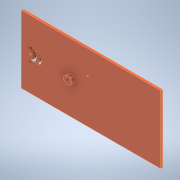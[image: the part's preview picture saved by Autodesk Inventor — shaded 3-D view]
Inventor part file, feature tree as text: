
AUTODESK INVENTOR PART (.ipt)
format: ipt  version: 2022.2 (Build 262287010, 287A)  size: 254,976 bytes
history: native  units: mm
features: extrude x15, sketch x9, other x1, plane x1
ambient origin geometry x8: Origin, YZ Plane, XZ Plane, XY Plane, X Axis, Y Axis, Z Axis, Center Point
bodies: Body1 (feature_tree)
feature tree (26):
  other  "Sólido1"
  extrude  "Extrusión1"  Depth=170.0mm
  extrude  "Extrusión4"  Depth=5.0mm
  extrude  "Extrusión5"  Depth=85.0mm
  extrude  "Extrusión6"  Depth=5.25mm
  sketch  "Boceto10"  dims[d26=4.0mm d27=0.0mm d29=50.0mm]
  plane  "Plano de trabajo1"
  extrude  "Extrusión10"  Depth=4.0mm
  extrude  "Extrusión11"  Depth=134.19mm
  extrude  "Extrusión12"  Depth=25.0mm
  extrude  "Extrusión13"  Depth=3.0mm
  extrude  "Extrusión14"  Depth=4.0mm
  extrude  "Extrusión15"  Depth=1.0mm
  extrude  "Extrusión22"  Depth=3.0mm TaperAngle=0.0deg
  extrude  "Extrusión23"  Depth=15.0mm
  extrude  "Extrusión24"  Depth=3.0mm
  extrude  "Extrusión25"  Depth=3.0mm
  extrude  "Extrusión26"  Depth=15.0mm
  sketch  "Boceto2"  dims[d0=260.0mm d1=170.0mm]
  sketch  "Boceto5"  dims[d2=5.0mm d3=0.0mm d7=5.25mm]
  sketch  "Boceto6"  dims[d8=19.75mm d14=85.0mm]
  sketch  "Boceto8"  dims[d23=10.5mm d25=5.25mm]
  sketch  "Boceto13"  dims[d31=35.0mm d32=134.19mm]
  sketch  "Boceto15"  dims[d35=40.0mm d36=25.0mm]
  sketch  "Boceto16"  dims[d38=4.0mm d39=3.0mm]
  sketch  "Boceto20"  dims[d40=1.4mm d41=0.0mm d42=4.0mm d43=1.0mm d44=2.0mm d45=0.0mm d51=15.0mm d57=37.0mm d58=40.0mm d59=15.0mm d60=12.5mm d61=6.0mm d62=12.5mm d63=6.0mm d64=3.0mm d65=3.0mm d66=1.5mm d67=0.0mm d68=3.0mm d69=3.0mm d70=0.0mm d71=0.0mm d72=5.0mm d73=0.0mm d75=10.0mm d76=0.0mm d77=10.0mm d78=0.0mm d79=0.0mm d80=148.0mm d82=40.0mm d83=5.0mm d84=4.0mm d85=0.0mm d87=80.0mm d88=30.0mm d102=35.0mm d115=90.0mm d116=5.0mm d117=0.0mm d118=0.0mm d119=0.0mm d121=5.0mm d122=0.0mm d126=15.0mm d127=6.0mm d128=6.0mm d129=1.5mm d130=1.5mm d131=1.5mm d132=0.0mm d133=0.0mm d134=0.0mm d135=3.0mm d137=38.749197mm d138=98.63376mm d46=0.5mm d47=0.872665mm d74=0.5mm d98=0.5mm d99=0.872665mm d100=0.5mm d101=0.872665mm d103=0.5mm d104=0.872665mm d105=0.5mm d106=0.872665mm d107=0.5mm d108=0.872665mm d109=0.5mm d110=0.872665mm d120=0.5mm]
